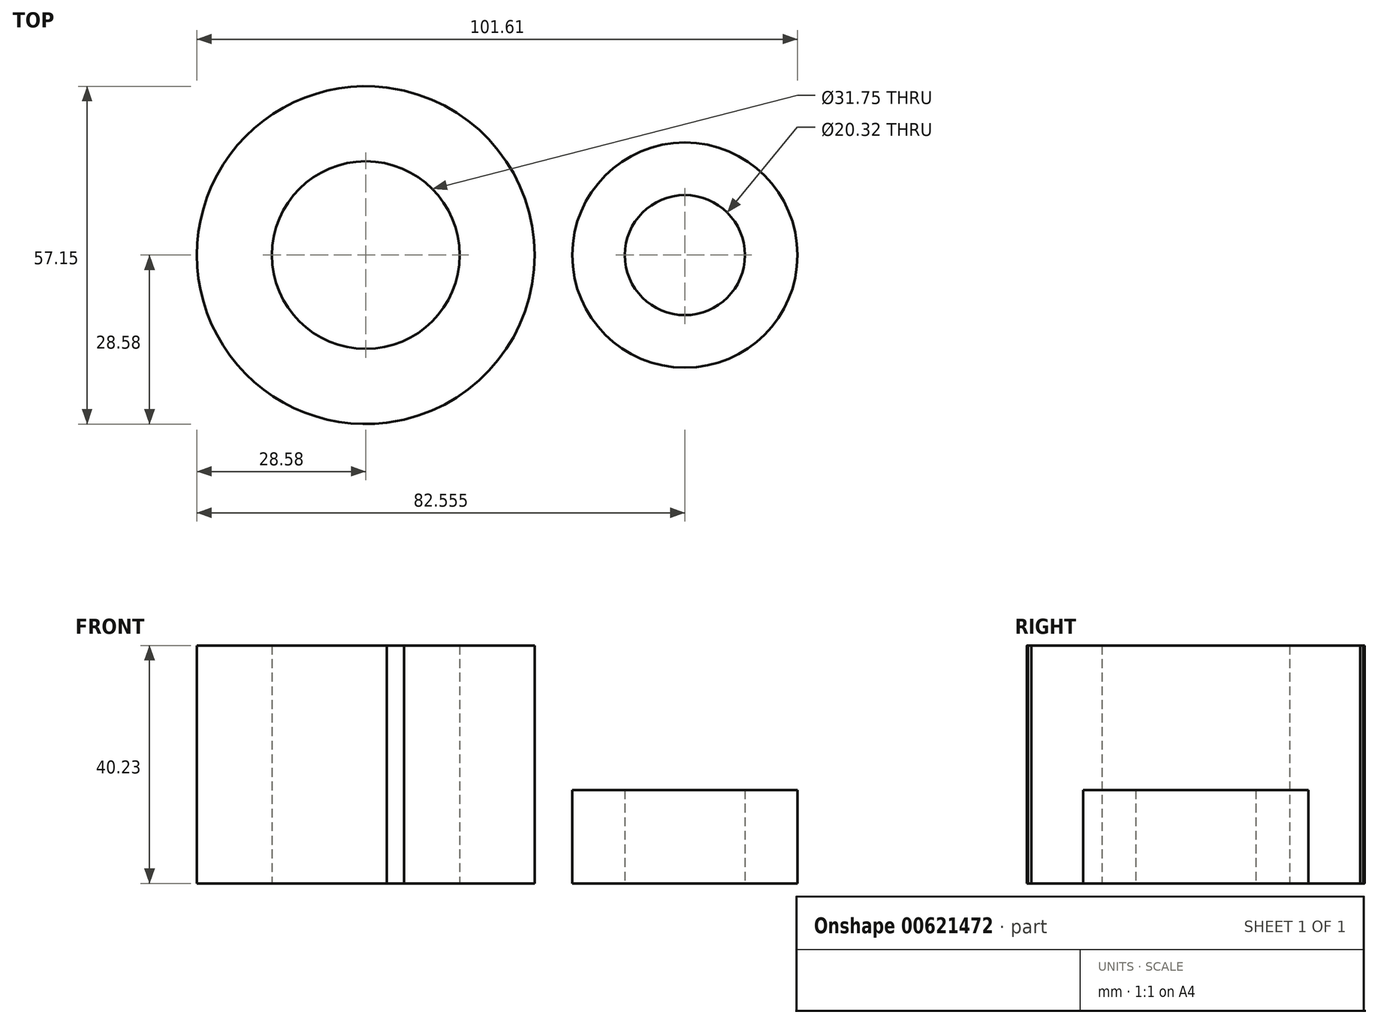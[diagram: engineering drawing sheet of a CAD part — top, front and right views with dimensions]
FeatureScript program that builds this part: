
annotation { "Feature Type Name" : "Feature", "Feature Type Description" : "" }
export const myFeature = defineFeature(function(context is Context, id is Id, definition is map)
    precondition{}
    {
        {
            var Q0;
            Q0=qCreatedBy(makeId("Top.planeOp"),FACE);
            var sketch = newSketch(context, id + "F0", { "sketchPlane" : qUnion([Q0])});
            skCircle(sketch, "E0", {"center": v(0, 0) * mm, "radius": 28.58 * mm});
            skCircle(sketch, "E1", {"center": v(0, 0) * mm, "radius": 15.88 * mm});
            skLineSegment(sketch, "E2", {"start": v(0, 0) * mm, "end": v(53.97, 0) * mm, "construction": true});
            skCircle(sketch, "E3", {"center": v(53.97, 0) * mm, "radius": 19.05 * mm});
            skCircle(sketch, "E4", {"center": v(53.97, 0) * mm, "radius": 10.16 * mm});
            skLineSegment(sketch, "E5", {"start": v(3.56, -28.35) * mm, "end": v(57.32, -18.75) * mm});
            skLineSegment(sketch, "E6", {"start": v(3.56, 28.35) * mm, "end": v(57.32, 18.75) * mm});
            skSolve(sketch);
        }
        {
            var Q0;
            {var subQ0=sQuery(id+"F0.wireOp",EDGE,"E6");var subQ1=sQuery(id+"F0.wireOp",EDGE,"E0");var subQ2=makeQuery(id+"F0.imprint","INTERSECT",VERTEX,{"disambiguationData":[OD(1.0)],"derivedFrom":[subQ1,subQ0]});Q0=makeQuery(id+"F0.imprint","IMPRINT",FACE,{"disambiguationData":[TD([[makeQuery(id+"F0.imprint","IMPRINT",EDGE,{"disambiguationData":[TD([[subQ2,1.0]])],"derivedFrom":subQ1}),-1.0]])]});}
            var Q1;
            Q1=makeQuery(id+"F0.imprint","IMPRINT",FACE,{"disambiguationData":[TD([[makeQuery(id+"F0.imprint","IMPRINT",EDGE,{"derivedFrom":sQuery(id+"F0.wireOp",EDGE,"E4")}),-1.0]])]});
            var Q2;
            Q2=makeQuery(id+"F0.imprint","IMPRINT",FACE,{"disambiguationData":[TD([[makeQuery(id+"F0.imprint","IMPRINT",EDGE,{"derivedFrom":sQuery(id+"F0.wireOp",EDGE,"E1")}),-1.0]])]});
            extrude(context, id + "F1", {"entities" : qUnion([Q0, Q1, Q2]), "depth" : 15.77 * mm, "offsetDistance" : 25.4 * mm});
        }
        {
            var Q0;
            Q0=makeQuery(id+"F1.opExtrude","CAP_FACE",FACE,{"disambiguationData":[OSD([sQuery(id+"F0.wireOp",EDGE,"E0"),sQuery(id+"F0.wireOp",EDGE,"E1"),sQuery(id+"F0.wireOp",EDGE,"E3"),sQuery(id+"F0.wireOp",EDGE,"E4"),sQuery(id+"F0.wireOp",EDGE,"E5"),sQuery(id+"F0.wireOp",EDGE,"E6")])],"isStart":false});
            var sketch = newSketch(context, id + "F2", { "sketchPlane" : qUnion([Q0])});
            skCircle(sketch, "E7", {"center": v(0, 0) * mm, "radius": 15.88 * mm});
            skCircle(sketch, "E8", {"center": v(0, 0) * mm, "radius": 28.58 * mm});
            skSolve(sketch);
        }
        {
            var Q0;
            Q0=makeQuery(id+"F2.imprint","IMPRINT",FACE,{"disambiguationData":[TD([[makeQuery(id+"F2.imprint","IMPRINT",EDGE,{"derivedFrom":sQuery(id+"F2.wireOp",EDGE,"E7")}),-1.0]])]});
            extrude(context, id + "F3", {"entities" : qUnion([Q0]), "operationType" : NewBodyOperationType.ADD, "depth" : 24.46 * mm, "offsetDistance" : 25.4 * mm});
        }
    });
